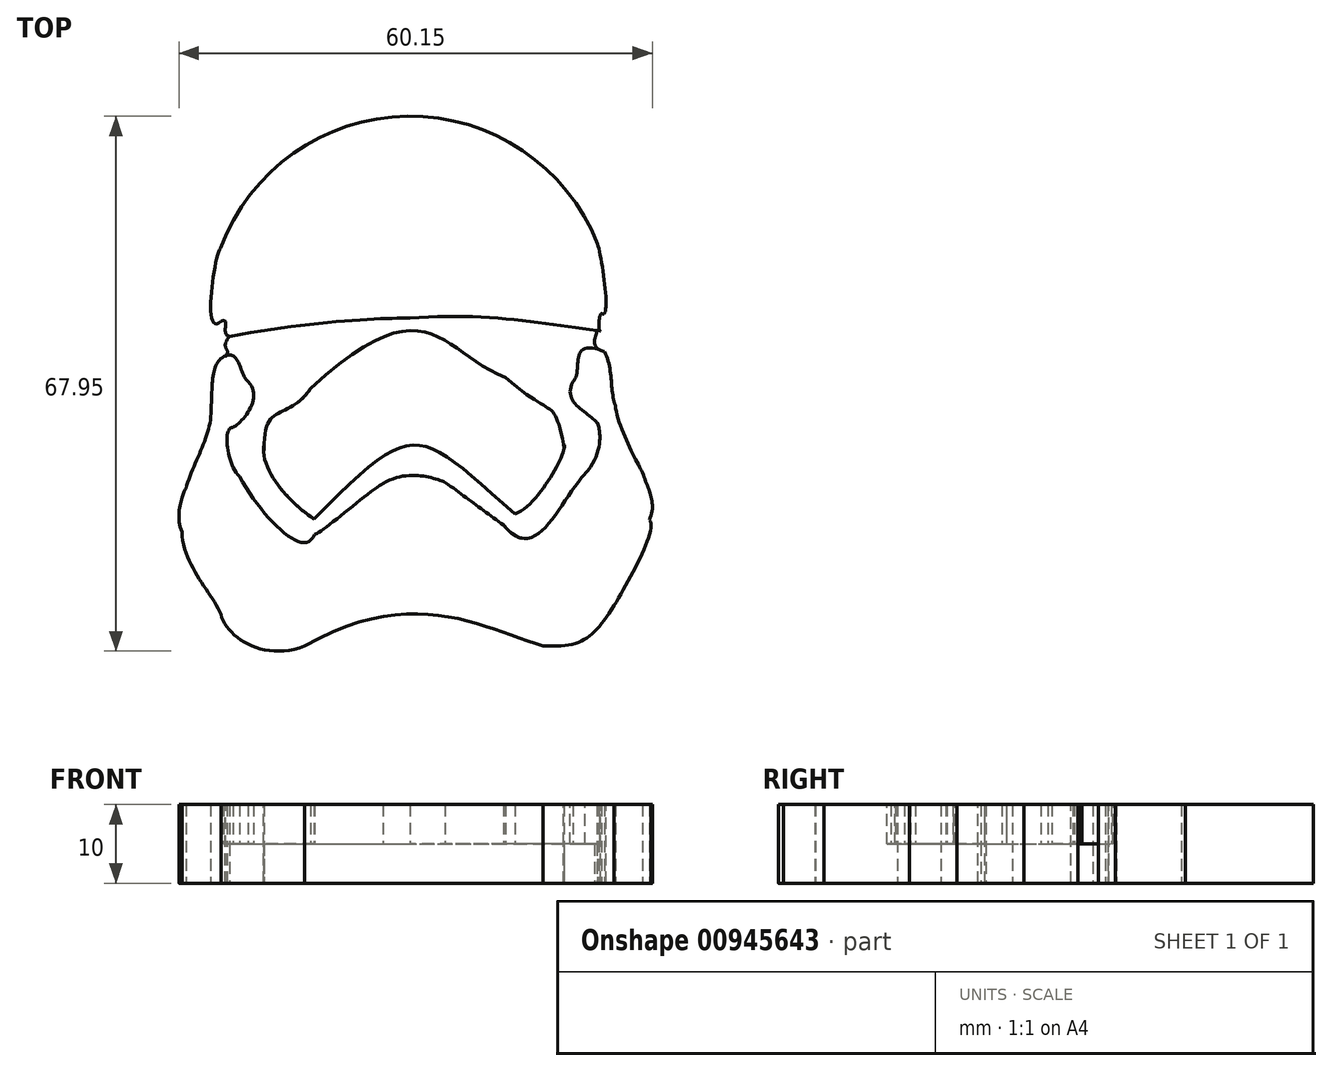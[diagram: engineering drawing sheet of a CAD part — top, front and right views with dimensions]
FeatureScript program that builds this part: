
annotation { "Feature Type Name" : "Feature", "Feature Type Description" : "" }
export const myFeature = defineFeature(function(context is Context, id is Id, definition is map)
    precondition{}
    {
        {
            var Q0;
            Q0=qCreatedBy(makeId("Top.planeOp"),FACE);
            var sketch = newSketch(context, id + "F0", { "sketchPlane" : qUnion([Q0])});
            skFitSpline(sketch, "E0", {"points": [v(-58.12, -55.62) * mm, v(-27.84, -55.6) * mm], "startDerivative": vector(42.4, 24.06) * mm, "endDerivative": vector(22.87, -6.3) * mm});
            skFitSpline(sketch, "E1", {"points": [v(-65.1, -16.53) * mm, v(-57.36, -22.9) * mm], "startDerivative": vector(1.31, -6.12) * mm, "endDerivative": vector(22.14, 12.36) * mm});
            skFitSpline(sketch, "E2", {"points": [v(-24.5, -16.06) * mm, v(-32.62, -21.5) * mm], "startDerivative": vector(0.31, -14.21) * mm, "endDerivative": vector(-16.67, 12.88) * mm});
            skFitSpline(sketch, "E3", {"points": [v(-57.36, -22.9) * mm, v(-32.62, -21.5) * mm], "startDerivative": vector(44.89, 41.51) * mm, "endDerivative": vector(24.42, -9.13) * mm});
            skFitSpline(sketch, "E4", {"points": [v(-56.92, -39.48) * mm, v(-31.4, -38.88) * mm], "startDerivative": vector(39.02, 39.76) * mm, "endDerivative": vector(37.54, -32.84) * mm});
            skArc(sketch, "E5", {"start": v(-20.92, -4.55) * mm, "mid": v(-45.05, 11.67) * mm, "end": v(-68.82, -5.08) * mm});
            skFitSpline(sketch, "E6", {"points": [v(-68.82, -5.08) * mm, v(-68.82, -14.4) * mm], "startDerivative": vector(-2.57, -3.62) * mm, "endDerivative": vector(6.97, 6.6) * mm});
            skFitSpline(sketch, "E7", {"points": [v(-20.92, -4.55) * mm, v(-20.4, -13.43) * mm], "startDerivative": vector(1.58, -5.49) * mm, "endDerivative": vector(-3.79, 2.2) * mm});
            skFitSpline(sketch, "E8", {"points": [v(-68.82, -14.4) * mm, v(-20.4, -13.43) * mm], "startDerivative": vector(47.02, 13.79) * mm, "endDerivative": vector(25.44, -8.82) * mm});
            skFitSpline(sketch, "E9", {"points": [v(-58.12, -55.62) * mm, v(-68.78, -51.62) * mm], "startDerivative": vector(-15.48, -6.06) * mm, "endDerivative": vector(-2.35, 8.95) * mm});
            skFitSpline(sketch, "E10", {"points": [v(-27.84, -55.6) * mm, v(-18.81, -50.5) * mm], "startDerivative": vector(14.75, -1.02) * mm, "endDerivative": vector(7.76, 12.24) * mm});
            skFitSpline(sketch, "E11", {"points": [v(-18.81, -50.5) * mm, v(-14.36, -39.65) * mm], "startDerivative": vector(5.87, 10.3) * mm, "endDerivative": vector(-3.4, 3.49) * mm});
            skFitSpline(sketch, "E12", {"points": [v(-68.78, -51.62) * mm, v(-73.73, -41.14) * mm], "startDerivative": vector(-3.7, 8.83) * mm, "endDerivative": vector(-0.45, 12.86) * mm});
            skFitSpline(sketch, "E13", {"points": [v(-14.36, -39.65) * mm, v(-15.22, -33.61) * mm], "startDerivative": vector(2.99, 7.05) * mm, "endDerivative": vector(-2.15, 6.7) * mm});
            skFitSpline(sketch, "E14", {"points": [v(-73.73, -41.14) * mm, v(-73.23, -35.63) * mm], "startDerivative": vector(-3, 6.9) * mm, "endDerivative": vector(0.8, 1.12) * mm});
            skFitSpline(sketch, "E15", {"points": [v(-73.23, -35.63) * mm, v(-70.07, -26.52) * mm], "startDerivative": vector(2.5, 9.08) * mm, "endDerivative": vector(0.7, 8.63) * mm});
            skFitSpline(sketch, "E16", {"points": [v(-15.22, -33.61) * mm, v(-18.67, -25.07) * mm], "startDerivative": vector(-1.14, 2.3) * mm, "endDerivative": vector(-0.93, 8.82) * mm});
            skFitSpline(sketch, "E17", {"points": [v(-18.67, -25.07) * mm, v(-20.03, -18.24) * mm], "startDerivative": vector(-2.09, 5.33) * mm, "endDerivative": vector(-3.32, 6.64) * mm});
            skFitSpline(sketch, "E18", {"points": [v(-70.07, -26.52) * mm, v(-68.8, -19.14) * mm], "startDerivative": vector(0.58, 11.34) * mm, "endDerivative": vector(3.68, 3.16) * mm});
            skFitSpline(sketch, "E19", {"points": [v(-67.68, -16.3) * mm, v(-68.82, -14.4) * mm], "startDerivative": vector(-3.8, 0.64) * mm, "endDerivative": vector(-4.26, -1.9) * mm});
            skFitSpline(sketch, "E20", {"points": [v(-20.54, -15.65) * mm, v(-20.4, -13.43) * mm], "startDerivative": vector(-1.48, 0.42) * mm, "endDerivative": vector(0.67, -1.37) * mm});
            skFitSpline(sketch, "E21", {"points": [v(-31.4, -38.88) * mm, v(-25.24, -30.03) * mm], "startDerivative": vector(10.33, 4.3) * mm, "endDerivative": vector(-2.49, -0.24) * mm});
            skFitSpline(sketch, "E22", {"points": [v(-56.92, -39.48) * mm, v(-63.27, -29.94) * mm], "startDerivative": vector(-5.15, 2.84) * mm, "endDerivative": vector(2.35, 11.55) * mm});
            skFitSpline(sketch, "E23", {"points": [v(-63.27, -29.94) * mm, v(-57.36, -22.9) * mm], "startDerivative": vector(0.45, 16.15) * mm, "endDerivative": vector(8.86, 12.72) * mm});
            skFitSpline(sketch, "E24", {"points": [v(-25.24, -30.03) * mm, v(-32.62, -21.5) * mm], "startDerivative": vector(-3.96, 18.82) * mm, "endDerivative": vector(-18.35, 16.36) * mm});
            skFitSpline(sketch, "E25", {"points": [v(-63.27, -29.94) * mm, v(-66.43, -34.11) * mm], "startDerivative": vector(0.13, -5.2) * mm, "endDerivative": vector(-7.06, 0.49) * mm});
            skFitSpline(sketch, "E26", {"points": [v(-25.24, -30.03) * mm, v(-22.53, -33.76) * mm], "startDerivative": vector(0.44, -7.68) * mm, "endDerivative": vector(-1.9, -1.92) * mm});
            skFitSpline(sketch, "E27", {"points": [v(-66.43, -34.11) * mm, v(-56.89, -41.44) * mm], "startDerivative": vector(9.26, -16.23) * mm, "endDerivative": vector(3.84, 10.12) * mm});
            skFitSpline(sketch, "E28", {"points": [v(-22.53, -33.76) * mm, v(-32.87, -40.28) * mm], "startDerivative": vector(-9.93, -10.65) * mm, "endDerivative": vector(-12.73, 15.7) * mm});
            skFitSpline(sketch, "E29", {"points": [v(-56.89, -41.44) * mm, v(-48.17, -34.98) * mm], "startDerivative": vector(1.95, -0.39) * mm, "endDerivative": vector(4.28, 1.87) * mm});
            skFitSpline(sketch, "E30", {"points": [v(-32.87, -40.28) * mm, v(-40.27, -34.84) * mm], "startDerivative": vector(-7.4, 5.44) * mm, "endDerivative": vector(-8.03, 5.83) * mm});
            skFitSpline(sketch, "E31", {"points": [v(-48.17, -34.98) * mm, v(-40.27, -34.84) * mm], "startDerivative": vector(9.85, 5.66) * mm, "endDerivative": vector(4.67, -1.69) * mm});
            skLineSegment(sketch, "E32", {"start": v(-67.68, -16.3) * mm, "end": v(-65.1, -16.53) * mm});
            skLineSegment(sketch, "E33", {"start": v(-24.5, -16.06) * mm, "end": v(-20.54, -15.65) * mm});
            skFitSpline(sketch, "E34", {"points": [v(-66.43, -34.11) * mm, v(-67.26, -27.86) * mm], "startDerivative": vector(-5.18, 5.46) * mm, "endDerivative": vector(3.73, -0.41) * mm});
            skFitSpline(sketch, "E35", {"points": [v(-22.53, -33.76) * mm, v(-21, -27.31) * mm], "startDerivative": vector(8.95, 9.81) * mm, "endDerivative": vector(0, -1.66) * mm});
            skFitSpline(sketch, "E36", {"points": [v(-67.26, -27.86) * mm, v(-65.32, -22.06) * mm], "startDerivative": vector(3.53, 1.66) * mm, "endDerivative": vector(-6.02, 6.02) * mm});
            skFitSpline(sketch, "E37", {"points": [v(-21, -27.31) * mm, v(-24.04, -22.06) * mm], "startDerivative": vector(-3.11, 4.15) * mm, "endDerivative": vector(4.56, 8.1) * mm});
            skFitSpline(sketch, "E38", {"points": [v(-65.32, -22.06) * mm, v(-68.8, -19.14) * mm], "startDerivative": vector(-3.48, 2.92) * mm, "endDerivative": vector(-7.32, -5.27) * mm});
            skFitSpline(sketch, "E39", {"points": [v(-24.04, -22.06) * mm, v(-20.03, -18.24) * mm], "startDerivative": vector(4, 3.82) * mm, "endDerivative": vector(14.44, -5.82) * mm});
            skFitSpline(sketch, "E40", {"points": [v(-67.68, -16.3) * mm, v(-44.77, -13.97) * mm], "startDerivative": vector(31.16, 5.97) * mm, "endDerivative": vector(10.2, 0) * mm});
            skFitSpline(sketch, "E41", {"points": [v(-20.54, -15.65) * mm, v(-44.77, -13.97) * mm], "startDerivative": vector(-20.86, 2.98) * mm, "endDerivative": vector(-28.18, -2.29) * mm});
            skFitSpline(sketch, "E42", {"points": [v(-68.8, -19.14) * mm, v(-67.68, -16.3) * mm], "startDerivative": vector(6.37, 3.73) * mm, "endDerivative": vector(4.67, 5.88) * mm});
            skFitSpline(sketch, "E43", {"points": [v(-20.03, -18.24) * mm, v(-21.03, -15.51) * mm], "startDerivative": vector(-6.66, 1.6) * mm, "endDerivative": vector(-0.37, 1.94) * mm});
            skSolve(sketch);
        }
        {
            var Q0;
            Q0=makeQuery(id+"F0.imprint","IMPRINT",FACE,{"disambiguationData":[TD([[makeQuery(id+"F0.imprint","IMPRINT",EDGE,{"derivedFrom":sQuery(id+"F0.wireOp",EDGE,"E0")}),1.0]])]});
            var Q1;
            Q1=makeQuery(id+"F0.imprint","IMPRINT",FACE,{"disambiguationData":[TD([[makeQuery(id+"F0.imprint","IMPRINT",EDGE,{"derivedFrom":sQuery(id+"F0.wireOp",EDGE,"E3")}),-1.0]])]});
            var Q2;
            {var subQ0=sQuery(id+"F0.wireOp",EDGE,"E40");Q2=makeQuery(id+"F0.imprint","IMPRINT",FACE,{"disambiguationData":[TD([[makeQuery(id+"F0.imprint","IMPRINT",EDGE,{"derivedFrom":subQ0}),1.0]])]});}
            var Q3;
            Q3=makeQuery(id+"F0.imprint","IMPRINT",FACE,{"disambiguationData":[TD([[makeQuery(id+"F0.imprint","IMPRINT",EDGE,{"derivedFrom":sQuery(id+"F0.wireOp",EDGE,"E5")}),1.0]])]});
            extrude(context, id + "F1", {"entities" : qUnion([Q0, Q1, Q2, Q3]), "depth" : 10 * mm, "offsetDistance" : 25 * mm});
        }
        {
            var Q0;
            {var subQ8=sQuery(id+"F0.wireOp",EDGE,"E2");Q0=makeQuery(id+"F0.imprint","IMPRINT",FACE,{"disambiguationData":[TD([[makeQuery(id+"F0.imprint","IMPRINT",EDGE,{"derivedFrom":subQ8}),1.0]])]});}
            var Q1;
            {var subQ6=sQuery(id+"F0.wireOp",EDGE,"E4");Q1=makeQuery(id+"F0.imprint","IMPRINT",FACE,{"disambiguationData":[TD([[makeQuery(id+"F0.imprint","IMPRINT",EDGE,{"derivedFrom":subQ6}),-1.0]])]});}
            var Q2;
            Q2=makeQuery(id+"F0.imprint","IMPRINT",FACE,{"disambiguationData":[TD([[makeQuery(id+"F0.imprint","IMPRINT",EDGE,{"derivedFrom":sQuery(id+"F0.wireOp",EDGE,"E1")}),-1.0]])]});
            var Q3;
            Q3=makeQuery(id+"F0.imprint","IMPRINT",FACE,{"disambiguationData":[TD([[makeQuery(id+"F0.imprint","IMPRINT",EDGE,{"derivedFrom":sQuery(id+"F0.wireOp",EDGE,"E1")}),1.0]])]});
            extrude(context, id + "F2", {"entities" : qUnion([Q0, Q1, Q2, Q3]), "operationType" : NewBodyOperationType.ADD, "depth" : 5 * mm, "offsetDistance" : 25 * mm});
        }
    });
